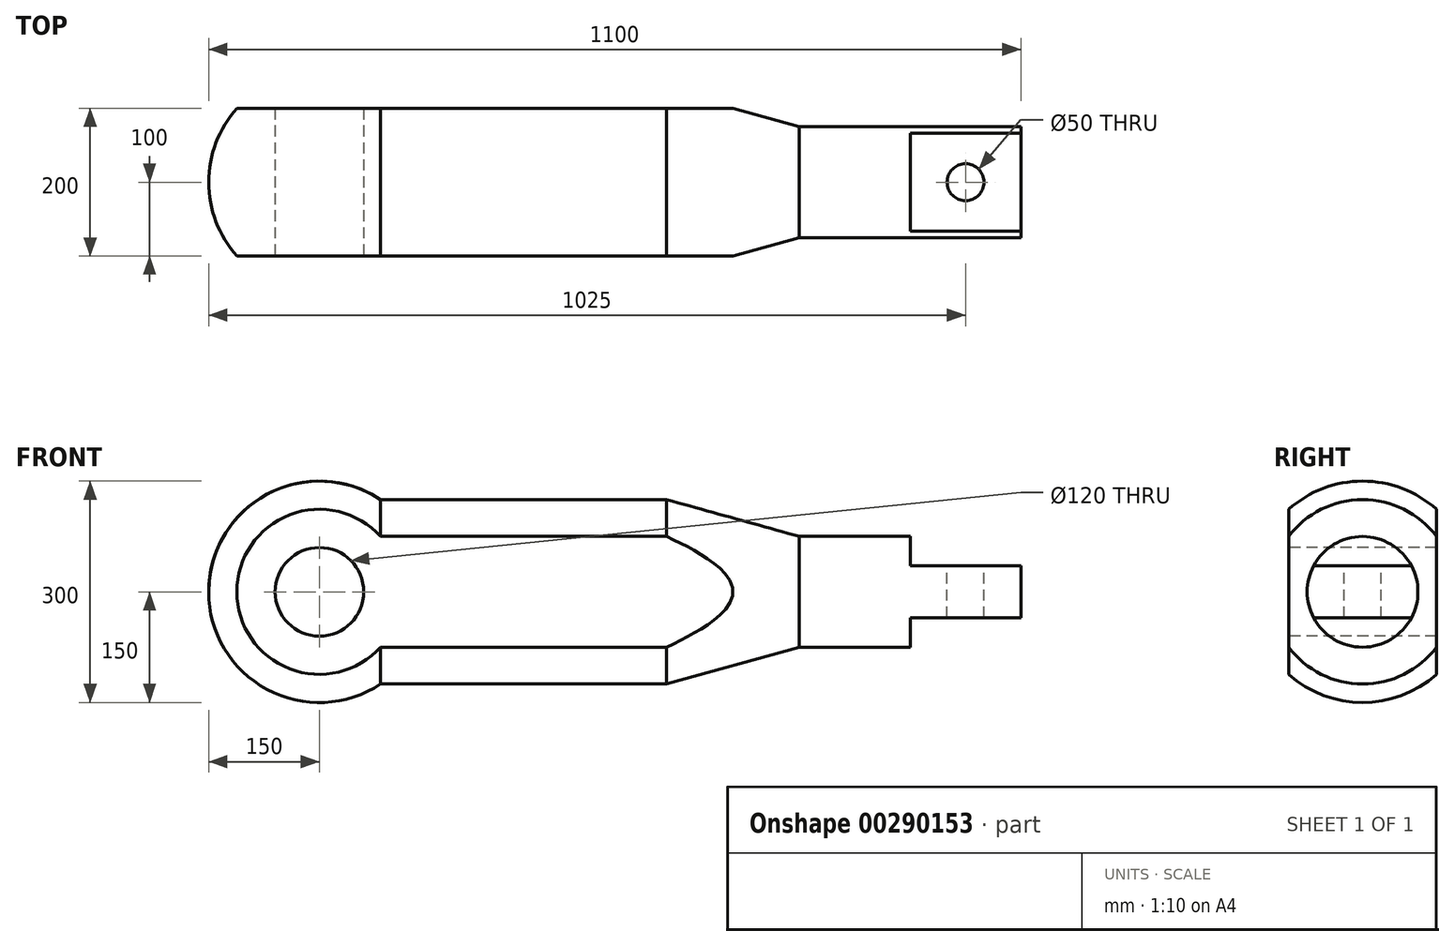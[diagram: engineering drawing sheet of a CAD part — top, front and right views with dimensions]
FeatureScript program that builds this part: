
annotation { "Feature Type Name" : "Feature", "Feature Type Description" : "" }
export const myFeature = defineFeature(function(context is Context, id is Id, definition is map)
    precondition{}
    {
        {
            var Q0;
            Q0=qCreatedBy(makeId("Front.planeOp"),FACE);
            var sketch = newSketch(context, id + "F0", { "sketchPlane" : qUnion([Q0])});
            skLineSegment(sketch, "E0.bottom", {"start": v(800, 35) * mm, "end": v(950, 35) * mm});
            skLineSegment(sketch, "E0.top", {"start": v(800, 75) * mm, "end": v(950, 75) * mm});
            skLineSegment(sketch, "E0.left", {"start": v(800, 35) * mm, "end": v(800, 75) * mm});
            skLineSegment(sketch, "E0.right", {"start": v(950, 35) * mm, "end": v(950, 75) * mm});
            skLineSegment(sketch, "E1.MirrorCS", {"start": v(800, -35) * mm, "end": v(800, -75) * mm});
            skLineSegment(sketch, "E2.MirrorCS", {"start": v(800, -35) * mm, "end": v(950, -35) * mm});
            skLineSegment(sketch, "E3.MirrorCS", {"start": v(950, -35) * mm, "end": v(950, -75) * mm});
            skLineSegment(sketch, "E4.MirrorCS", {"start": v(800, -75) * mm, "end": v(950, -75) * mm});
            skSolve(sketch);
        }
        {
            var Q0;
            Q0=qCreatedBy(makeId("Top.planeOp"),FACE);
            var sketch = newSketch(context, id + "F1", { "sketchPlane" : qUnion([Q0])});
            skCircle(sketch, "E5", {"center": v(875, 0) * mm, "radius": 25 * mm});
            skSolve(sketch);
        }
        {
            var Q0;
            Q0=qCreatedBy(makeId("Right.planeOp"),FACE);
            var sketch = newSketch(context, id + "F2", { "sketchPlane" : qUnion([Q0])});
            skLineSegment(sketch, "E6.bottom", {"start": v(-100, -150) * mm, "end": v(-150, -150) * mm});
            skLineSegment(sketch, "E6.top", {"start": v(-100, 150) * mm, "end": v(-150, 150) * mm});
            skLineSegment(sketch, "E6.left", {"start": v(-100, -150) * mm, "end": v(-100, 150) * mm});
            skLineSegment(sketch, "E6.right", {"start": v(-150, -150) * mm, "end": v(-150, 150) * mm});
            skPoint(sketch, "E7", {"position": v(-100, 0) * mm});
            skLineSegment(sketch, "E8.MirrorCS", {"start": v(100, 150) * mm, "end": v(150, 150) * mm});
            skLineSegment(sketch, "E9.MirrorCS", {"start": v(100, -150) * mm, "end": v(100, 150) * mm});
            skLineSegment(sketch, "E10.MirrorCS", {"start": v(150, -150) * mm, "end": v(150, 150) * mm});
            skLineSegment(sketch, "E11.MirrorCS", {"start": v(100, -150) * mm, "end": v(150, -150) * mm});
            skSolve(sketch);
        }
        {
            var Q0;
            Q0=qCreatedBy(makeId("Front.planeOp"),FACE);
            var sketch = newSketch(context, id + "F3", { "sketchPlane" : qUnion([Q0])});
            skCircle(sketch, "E12", {"center": v(0, 0) * mm, "radius": 60 * mm});
            skSolve(sketch);
        }
        {
            var Q0;
            Q0=qCreatedBy(makeId("Front.planeOp"),FACE);
            var sketch = newSketch(context, id + "F4", { "sketchPlane" : qUnion([Q0])});
            skArc(sketch, "E13", {"start": v(82.92, 125) * mm, "mid": v(-150, 0) * mm, "end": v(82.92, -125) * mm});
            skLineSegment(sketch, "E14.bottom", {"start": v(82.92, 125) * mm, "end": v(470, 125) * mm});
            skLineSegment(sketch, "E14.top", {"start": v(82.92, -125) * mm, "end": v(470, -125) * mm});
            skLineSegment(sketch, "E15", {"start": v(470, 125) * mm, "end": v(650, 75) * mm});
            skLineSegment(sketch, "E16.MirrorCS", {"start": v(470, -125) * mm, "end": v(650, -75) * mm});
            skLineSegment(sketch, "E17.bottom", {"start": v(650, 75) * mm, "end": v(950, 75) * mm});
            skLineSegment(sketch, "E17.top", {"start": v(650, -75) * mm, "end": v(950, -75) * mm});
            skLineSegment(sketch, "E17.right", {"start": v(950, 75) * mm, "end": v(950, -75) * mm});
            skPoint(sketch, "E18.orphan", {"position": v(0, 125) * mm});
            skPoint(sketch, "E19.orphan", {"position": v(0, -125) * mm});
            skLineSegment(sketch, "E20", {"start": v(-150, 0) * mm, "end": v(950, 0) * mm});
            skSolve(sketch);
        }
        {
            var Q0;
            {var subQ1=sQuery(id+"F4.wireOp",EDGE,"E14.bottom");Q0=makeQuery(id+"F4.imprint","IMPRINT",FACE,{"disambiguationData":[TD([[makeQuery(id+"F4.imprint","IMPRINT",EDGE,{"derivedFrom":subQ1}),-1.0]])]});}
            var Q1;
            Q1=sQuery(id+"F4.wireOp",EDGE,"E20");
            revolve(context, id + "F5", {"entities" : qUnion([Q0]), "axis" : qUnion([Q1]), "revolveType" : RevolveType.FULL});
        }
        {
            var Q0;
            Q0 = qSketchRegion(id + "F3", true);
            extrude(context, id + "F6", {"entities" : qUnion([Q0]), "operationType" : NewBodyOperationType.REMOVE, "endBound" : BoundingType.SYMMETRIC, "oppositeDirection" : true, "depth" : 500 * mm});
        }
        {
            var Q0;
            Q0 = qSketchRegion(id + "F2", true);
            extrude(context, id + "F7", {"entities" : qUnion([Q0]), "operationType" : NewBodyOperationType.REMOVE, "endBound" : BoundingType.SYMMETRIC, "oppositeDirection" : true, "depth" : 1250 * mm});
        }
        {
            var Q0;
            Q0 = qSketchRegion(id + "F0", true);
            extrude(context, id + "F8", {"entities" : qUnion([Q0]), "operationType" : NewBodyOperationType.REMOVE, "endBound" : BoundingType.SYMMETRIC, "depth" : 150 * mm});
        }
        {
            var Q0;
            Q0 = qSketchRegion(id + "F1", true);
            extrude(context, id + "F9", {"entities" : qUnion([Q0]), "operationType" : NewBodyOperationType.REMOVE, "endBound" : BoundingType.SYMMETRIC, "oppositeDirection" : true, "depth" : 70 * mm});
        }
    });
